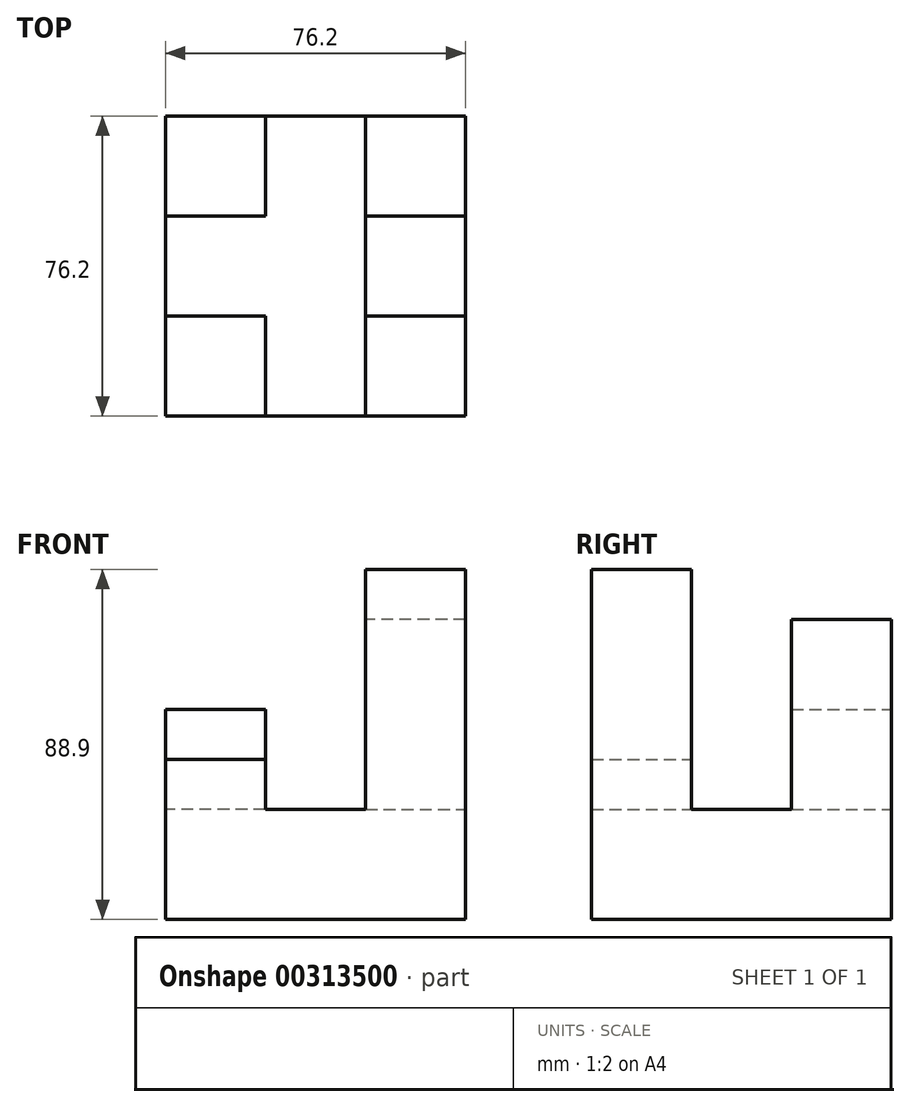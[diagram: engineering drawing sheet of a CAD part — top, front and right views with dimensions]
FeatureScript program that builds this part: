
annotation { "Feature Type Name" : "Feature", "Feature Type Description" : "" }
export const myFeature = defineFeature(function(context is Context, id is Id, definition is map)
    precondition{}
    {
        {
            var Q0;
            Q0=qCreatedBy(makeId("Front.planeOp"),FACE);
            var sketch = newSketch(context, id + "F0", { "sketchPlane" : qUnion([Q0])});
            skLineSegment(sketch, "E0", {"start": v(-60.67, -29.72) * mm, "end": v(15.53, -29.72) * mm});
            skLineSegment(sketch, "E1", {"start": v(15.53, -29.72) * mm, "end": v(15.53, 33.78) * mm});
            skLineSegment(sketch, "E2", {"start": v(15.53, 33.78) * mm, "end": v(-9.87, 33.78) * mm});
            skLineSegment(sketch, "E3", {"start": v(-9.87, 33.78) * mm, "end": v(-9.87, -1.71) * mm});
            skLineSegment(sketch, "E4", {"start": v(-9.87, -1.71) * mm, "end": v(-35.27, -1.71) * mm});
            skLineSegment(sketch, "E5", {"start": v(-42.65, -4.33) * mm, "end": v(-43.05, -4.33) * mm});
            skLineSegment(sketch, "E6", {"start": v(-35.27, -1.71) * mm, "end": v(-35.27, 10.99) * mm});
            skLineSegment(sketch, "E7", {"start": v(-35.27, 10.99) * mm, "end": v(-60.67, 10.99) * mm});
            skLineSegment(sketch, "E8", {"start": v(-60.67, 10.99) * mm, "end": v(-60.67, -29.72) * mm});
            skSolve(sketch);
        }
        {
            var Q0;
            Q0 = qSketchRegion(id + "F0", true);
            extrude(context, id + "F1", {"entities" : qUnion([Q0]), "depth" : 76.2 * mm});
        }
        {
            var Q0;
            Q0=makeQuery(id+"F1.opExtrude","SWEPT_FACE",FACE,{"disambiguationData":[OSD([sQuery(id+"F0.wireOp",EDGE,"E2")])]});
            var sketch = newSketch(context, id + "F2", { "sketchPlane" : qUnion([Q0])});
            skLineSegment(sketch, "E9", {"start": v(-9.87, 0) * mm, "end": v(-9.87, -25.4) * mm});
            skLineSegment(sketch, "E10", {"start": v(-9.87, -76.2) * mm, "end": v(-9.87, -50.8) * mm});
            skLineSegment(sketch, "E11", {"start": v(-9.87, -25.4) * mm, "end": v(15.53, -25.4) * mm});
            skLineSegment(sketch, "E12", {"start": v(-9.87, -50.8) * mm, "end": v(15.53, -50.8) * mm});
            skLineSegment(sketch, "E13", {"start": v(-34.24, 0) * mm, "end": v(-34.24, -25.4) * mm});
            skLineSegment(sketch, "E14", {"start": v(-35.17, -76.02) * mm, "end": v(-35.17, -50.62) * mm});
            skLineSegment(sketch, "E15", {"start": v(-34.24, -25.4) * mm, "end": v(-59.64, -25.4) * mm});
            skLineSegment(sketch, "E16", {"start": v(-35.17, -50.62) * mm, "end": v(-60.57, -50.62) * mm});
            skSolve(sketch);
        }
        {
            var Q0;
            {var subQ0=sQuery(id+"F2.wireOp",EDGE,"E11");Q0=makeQuery(id+"F2.imprint","IMPRINT",FACE,{"disambiguationData":[TD([[makeQuery(id+"F2.imprint","IMPRINT",EDGE,{"derivedFrom":subQ0}),-1.0]])]});}
            extrude(context, id + "F3", {"entities" : qUnion([Q0]), "operationType" : NewBodyOperationType.ADD, "oppositeDirection" : true, "depth" : 38.1 * mm});
        }
        {
            var Q0;
            Q0=makeQuery(id+"F1.opExtrude","SWEPT_FACE",FACE,{"disambiguationData":[OSD([sQuery(id+"F0.wireOp",EDGE,"E7")])]});
            var sketch = newSketch(context, id + "F4", { "sketchPlane" : qUnion([Q0])});
            skLineSegment(sketch, "E17", {"start": v(-35.27, 0) * mm, "end": v(-35.27, -25.4) * mm});
            skLineSegment(sketch, "E18", {"start": v(-35.27, -76.2) * mm, "end": v(-35.27, -50.8) * mm});
            skLineSegment(sketch, "E19", {"start": v(-35.27, -50.8) * mm, "end": v(-60.67, -50.8) * mm});
            skLineSegment(sketch, "E20", {"start": v(-35.27, -25.4) * mm, "end": v(-60.67, -25.4) * mm});
            skSolve(sketch);
        }
        {
            var Q0;
            {var subQ0=sQuery(id+"F4.wireOp",EDGE,"E19");Q0=makeQuery(id+"F4.imprint","IMPRINT",FACE,{"disambiguationData":[TD([[makeQuery(id+"F4.imprint","IMPRINT",EDGE,{"derivedFrom":subQ0}),-1.0]])]});}
            extrude(context, id + "F5", {"entities" : qUnion([Q0]), "operationType" : NewBodyOperationType.REMOVE, "oppositeDirection" : true, "depth" : 12.7 * mm});
        }
        {
            var Q0;
            {var subQ1=sQuery(id+"F0.wireOp",EDGE,"E7");Q0=makeQuery(id+"F5.boolean.opBoolean","SPLIT",FACE,{"disambiguationData":[TD([makeQuery(id+"F5.opExtrude","SWEPT_FACE",FACE,{"disambiguationData":[OSD([sQuery(id+"F4.wireOp",EDGE,"E20")])]})])],"derivedFrom":makeQuery(id+"F1.opExtrude","SWEPT_FACE",FACE,{"disambiguationData":[OSD([subQ1])]})});}
            extrude(context, id + "F6", {"entities" : qUnion([Q0]), "operationType" : NewBodyOperationType.ADD, "depth" : 12.7 * mm});
        }
        {
            var Q0;
            Q0=makeQuery(id+"F1.opExtrude","SWEPT_FACE",FACE,{"disambiguationData":[OSD([sQuery(id+"F0.wireOp",EDGE,"E2")])]});
            var sketch = newSketch(context, id + "F7", { "sketchPlane" : qUnion([Q0])});
            skLineSegment(sketch, "E21", {"start": v(-9.87, 0) * mm, "end": v(-9.87, -25.4) * mm});
            skLineSegment(sketch, "E22", {"start": v(-9.87, -76.2) * mm, "end": v(-9.87, -50.8) * mm});
            skLineSegment(sketch, "E23", {"start": v(-9.87, -50.8) * mm, "end": v(15.53, -50.8) * mm});
            skLineSegment(sketch, "E24", {"start": v(-9.87, -25.4) * mm, "end": v(15.53, -25.4) * mm});
            skSolve(sketch);
        }
        {
            var Q0;
            {var subQ0=sQuery(id+"F7.wireOp",EDGE,"E23");Q0=makeQuery(id+"F7.imprint","IMPRINT",FACE,{"disambiguationData":[TD([[makeQuery(id+"F7.imprint","IMPRINT",EDGE,{"derivedFrom":subQ0}),1.0]])]});}
            extrude(context, id + "F8", {"entities" : qUnion([Q0]), "operationType" : NewBodyOperationType.REMOVE, "oppositeDirection" : true, "depth" : 35.56 * mm});
        }
        {
            var Q0;
            {var subQ1=sQuery(id+"F0.wireOp",EDGE,"E2");Q0=makeQuery(id+"F8.boolean.opBoolean","SPLIT",FACE,{"disambiguationData":[TD([makeQuery(id+"F8.opExtrude","SWEPT_FACE",FACE,{"disambiguationData":[OSD([sQuery(id+"F7.wireOp",EDGE,"E23")])]})])],"derivedFrom":makeQuery(id+"F1.opExtrude","SWEPT_FACE",FACE,{"disambiguationData":[OSD([subQ1])]})});}
            extrude(context, id + "F9", {"entities" : qUnion([Q0]), "operationType" : NewBodyOperationType.ADD, "depth" : 25.4 * mm});
        }
        {
            var Q0;
            {var subQ2=sQuery(id+"F0.wireOp",EDGE,"E7");var subQ3=sQuery(id+"F0.wireOp",EDGE,"E2");Q0=makeQuery(id+"F8.boolean.opBoolean","SPLIT",FACE,{"disambiguationData":[TD([makeQuery(id+"F6.opExtrude","SWEPT_FACE",FACE,{"disambiguationData":[OSD([subQ2])]})])],"derivedFrom":makeQuery(id+"F1.opExtrude","SWEPT_FACE",FACE,{"disambiguationData":[OSD([subQ3])]})});}
            extrude(context, id + "F10", {"entities" : qUnion([Q0]), "operationType" : NewBodyOperationType.ADD, "depth" : 12.7 * mm});
        }
    });
